# Revit family: Firestop-Composite_Sheet-STI-Cable_Tray_Both_Sides_Of_Wall
name_source: partatom
category: Specialty Equipment
units: mm (PartAtom-declared; Revit-internal decimal feet)

## family parameters
Always vertical = Yes
Classification Number = 23.20.50.14.11
Cut with Voids When Loaded = No
Enable Cutting in Views = No
Host = Wall
Maintain Annotation Orientation = No
Part Type = Normal
Room Calculation Point = No
Round Connector Dimension = Use Diameter
Shared = No

## types (5) — shared parameters
Assembly Code = D4030900
Composite Sheet = Firestop-STI-CS-Composite_Sheet
Default Elevation = 0' - 0"
Fire Rating = Up to 4 Hr
Guide Specification = http://www.stifirestop.com
LEED Information = http://files.systems.stifirestop.com
Locate Distributor = http://www.stifirestop.com
MSDS = http://files.systems.stifirestop.com
Manufacturer = Specified Technologies Inc.
Manufacturer Fax No. = 908.526.9623
Model = Composite Sheet
Product Documentation Link = http://files.systems.stifirestop.com
Product Page URL = http://www.stifirestop.com
Tested Systems = https://systems.stifirestop.com
URL = http://www.stifirestop.com

## per-type parameters (varying)
| type | Description |
| CS1628 | Composite Sheet 16 x 28 in. (41 x 71 cm.) |
| CS2436 | Composite Sheet 24 x 36 in. (61 x 92 cm.) |
| CS3636 | Composite Sheet 36 x 36 in. (92 x 92 cm.) |
| CS3641 | Composite Sheet 36 x 41 in. (92 x 104 cm.) |
| CS2852 | Composite Sheet 28 x 52 in. (71 x 132 cm.) |

note: column(s) folded — value = type name in every type: Model Part

## geometry (parser evidence)
native form markers: Blend x6, Sweep x2
no freeform markers — native parametric forms only
